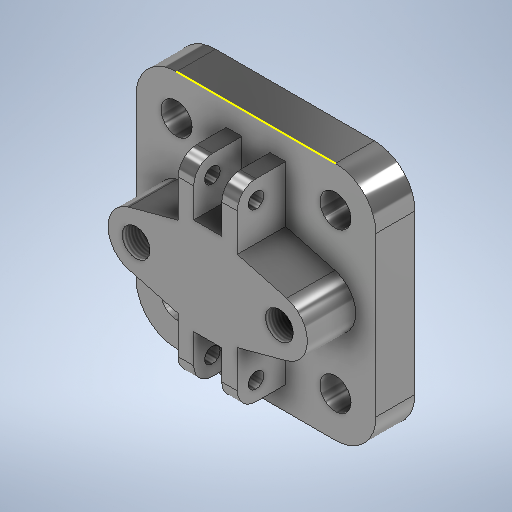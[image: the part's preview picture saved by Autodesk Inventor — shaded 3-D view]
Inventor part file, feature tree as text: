
AUTODESK INVENTOR PART (.ipt)
format: ipt  version: 2025.2 (Build 292293000, 293)  size: 372,736 bytes
history: native  units: mm
features: sketch x7, extrude x3, hole x3, fillet x1
ambient origin geometry x8: Origin, YZ Plane, XZ Plane, XY Plane, X Axis, Y Axis, Z Axis, Center Point
bodies: Solid1 (feature_tree)
feature tree (14):
  extrude  "Extrusion1"  Depth=154.0mm
  hole  "Hole1"  [1 undecoded]
  extrude  "Extrusion2"  Depth=6.0mm
  sketch  "Sketch4"  dims[d13=6.0mm d14=0.0mm d34=36.0mm]
  extrude  "Extrusion3"  Depth=6.0mm
  hole  "Hole2"  [1 undecoded]
  fillet  "Fillet1"  Radius=46.0mm
  hole  "Hole3"  [1 undecoded]
  sketch  "Sketch1"  dims[d0=154.0mm d1=154.0mm]
  sketch  "Sketch2"  dims[d2=26.0mm d3=25.0mm d4=0.0mm]
  sketch  "Sketch3"  dims[d5=20.0mm d6=6.0mm d7=4.0mm d8=2.0mm d9=90.0deg d10=8.0mm d11=20.594885mm d12=112.0mm]
  sketch  "Sketch5"  dims[d35=36.0mm d36=92.0mm d37=46.0mm]
  sketch  "Sketch6"  dims[d38=62.0mm d41=38.0mm]
  sketch  "Sketch7"  dims[d42=124.0mm d43=18.0mm d44=31.0mm d45=10.0mm d46=18.0mm d47=31.0mm d48=10.0mm d49=31.0mm d50=0.0mm d51=17.834936mm d52=22.0mm d53=4.0mm d54=2.0mm d55=90.0deg d56=26.0mm d57=20.594885mm d58=12.0mm d59=10.0mm d60=22.0mm d61=4.0mm d62=2.0mm d63=90.0deg d64=26.0mm d65=20.594885mm]
note: 3 required parameter values undecoded (feature->parameter linkage not recoverable at this tier; creation-order binding heuristic only, values carry confidence <= 0.55)
